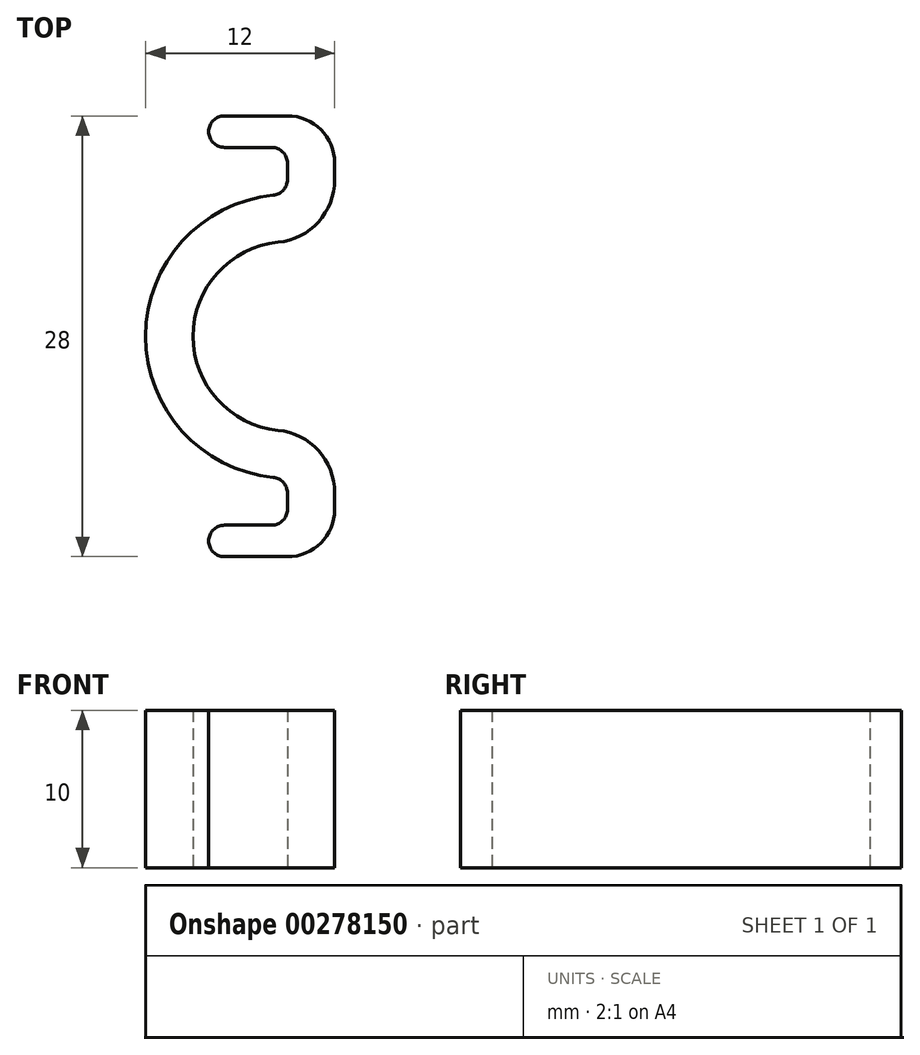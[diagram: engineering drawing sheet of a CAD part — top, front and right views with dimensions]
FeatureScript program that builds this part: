
annotation { "Feature Type Name" : "Feature", "Feature Type Description" : "" }
export const myFeature = defineFeature(function(context is Context, id is Id, definition is map)
    precondition{}
    {
        {
            var Q0;
            Q0=qCreatedBy(makeId("Top.planeOp"),FACE);
            var sketch = newSketch(context, id + "F0", { "sketchPlane" : qUnion([Q0])});
            skArc(sketch, "E0", {"start": v(0, 6) * mm, "mid": v(-6, 0) * mm, "end": v(0, -6) * mm});
            skArc(sketch, "E1.0", {"start": v(0, 9) * mm, "mid": v(-9, 0) * mm, "end": v(0, -9) * mm});
            skLineSegment(sketch, "E2", {"start": v(0, 9) * mm, "end": v(0, 6) * mm});
            skLineSegment(sketch, "E3", {"start": v(0, -6) * mm, "end": v(0, -9) * mm});
            skLineSegment(sketch, "E4.bottom", {"start": v(0, 6) * mm, "end": v(3, 6) * mm});
            skLineSegment(sketch, "E4.top", {"start": v(0, 14) * mm, "end": v(3, 14) * mm});
            skLineSegment(sketch, "E4.left", {"start": v(0, 6) * mm, "end": v(0, 14) * mm});
            skLineSegment(sketch, "E4.right", {"start": v(3, 6) * mm, "end": v(3, 14) * mm});
            skLineSegment(sketch, "E5.bottom", {"start": v(0, 14) * mm, "end": v(-5, 14) * mm});
            skLineSegment(sketch, "E5.top", {"start": v(0, 12) * mm, "end": v(-5, 12) * mm});
            skLineSegment(sketch, "E5.left", {"start": v(0, 14) * mm, "end": v(0, 12) * mm});
            skLineSegment(sketch, "E5.right", {"start": v(-5, 14) * mm, "end": v(-5, 12) * mm});
            skLineSegment(sketch, "E6.bottom", {"start": v(0, -6) * mm, "end": v(3, -6) * mm});
            skLineSegment(sketch, "E6.top", {"start": v(0, -14) * mm, "end": v(3, -14) * mm});
            skLineSegment(sketch, "E6.left", {"start": v(0, -6) * mm, "end": v(0, -14) * mm});
            skLineSegment(sketch, "E6.right", {"start": v(3, -6) * mm, "end": v(3, -14) * mm});
            skLineSegment(sketch, "E7.bottom", {"start": v(0, -14) * mm, "end": v(-5, -14) * mm});
            skLineSegment(sketch, "E7.top", {"start": v(0, -12) * mm, "end": v(-5, -12) * mm});
            skLineSegment(sketch, "E7.left", {"start": v(0, -14) * mm, "end": v(0, -12) * mm});
            skLineSegment(sketch, "E7.right", {"start": v(-5, -14) * mm, "end": v(-5, -12) * mm});
            skSolve(sketch);
        }
        {
            var Q0;
            {var subQ0=sQuery(id+"F0.wireOp",EDGE,"E0");Q0=makeQuery(id+"F0.imprint","IMPRINT",FACE,{"disambiguationData":[TD([[makeQuery(id+"F0.imprint","IMPRINT",EDGE,{"derivedFrom":subQ0}),-1.0]])]});}
            var Q1;
            {var subQ3=sQuery(id+"F0.wireOp",EDGE,"E4.bottom");Q1=makeQuery(id+"F0.imprint","IMPRINT",FACE,{"disambiguationData":[TD([[makeQuery(id+"F0.imprint","IMPRINT",EDGE,{"derivedFrom":subQ3}),1.0]])]});}
            var Q2;
            Q2=makeQuery(id+"F0.imprint","IMPRINT",FACE,{"disambiguationData":[TD([[makeQuery(id+"F0.imprint","IMPRINT",EDGE,{"derivedFrom":sQuery(id+"F0.wireOp",EDGE,"E5.bottom")}),1.0]])]});
            var Q3;
            {var subQ3=sQuery(id+"F0.wireOp",EDGE,"E6.bottom");Q3=makeQuery(id+"F0.imprint","IMPRINT",FACE,{"disambiguationData":[TD([[makeQuery(id+"F0.imprint","IMPRINT",EDGE,{"derivedFrom":subQ3}),-1.0]])]});}
            var Q4;
            Q4=makeQuery(id+"F0.imprint","IMPRINT",FACE,{"disambiguationData":[TD([[makeQuery(id+"F0.imprint","IMPRINT",EDGE,{"derivedFrom":sQuery(id+"F0.wireOp",EDGE,"E7.bottom")}),-1.0]])]});
            extrude(context, id + "F1", {"entities" : qUnion([Q0, Q1, Q2, Q3, Q4]), "depth" : 10 * mm});
        }
        {
            var Q0;
            Q0=makeQuery(id+"F1.opExtrude","SWEPT_EDGE",EDGE,{"disambiguationData":[OSD([sQuery(id+"F0.wireOp",EDGE,"E6.bottom"),sQuery(id+"F0.wireOp",EDGE,"E6.right")])]});
            var Q1;
            Q1=makeQuery(id+"F1.opExtrude","SWEPT_EDGE",EDGE,{"disambiguationData":[OSD([sQuery(id+"F0.wireOp",EDGE,"E4.bottom"),sQuery(id+"F0.wireOp",EDGE,"E4.right")])]});
            fillet(context, id + "F2", {"entities" : qUnion([Q0, Q1]), "radius" : 4 * mm, "tangentPropagation" : true, "allowEdgeOverflow" : false});
        }
        {
            var Q0;
            Q0=makeQuery(id+"F1.opExtrude","SWEPT_EDGE",EDGE,{"disambiguationData":[OSD([sQuery(id+"F0.wireOp",EDGE,"E6.top"),sQuery(id+"F0.wireOp",EDGE,"E6.right")])]});
            var Q1;
            Q1=makeQuery(id+"F1.opExtrude","SWEPT_EDGE",EDGE,{"disambiguationData":[OSD([sQuery(id+"F0.wireOp",EDGE,"E4.top"),sQuery(id+"F0.wireOp",EDGE,"E4.right")])]});
            fillet(context, id + "F3", {"entities" : qUnion([Q0, Q1]), "radius" : 3 * mm, "tangentPropagation" : true, "allowEdgeOverflow" : false});
        }
        {
            var Q0;
            Q0=makeQuery(id+"F1.opExtrude","SWEPT_EDGE",EDGE,{"disambiguationData":[OSD([sQuery(id+"F0.wireOp",EDGE,"E4.left"),sQuery(id+"F0.wireOp",EDGE,"E5.top"),sQuery(id+"F0.wireOp",EDGE,"E5.left")])]});
            var Q1;
            Q1=makeQuery(id+"F1.opExtrude","SWEPT_EDGE",EDGE,{"disambiguationData":[OSD([sQuery(id+"F0.wireOp",EDGE,"E6.left"),sQuery(id+"F0.wireOp",EDGE,"E7.top"),sQuery(id+"F0.wireOp",EDGE,"E7.left")])]});
            fillet(context, id + "F4", {"entities" : qUnion([Q0, Q1]), "radius" : 1 * mm, "tangentPropagation" : true, "allowEdgeOverflow" : false});
        }
        {
            var Q0;
            Q0=makeQuery(id+"F1.opExtrude","SWEPT_EDGE",EDGE,{"disambiguationData":[OSD([sQuery(id+"F0.wireOp",EDGE,"E1.0"),sQuery(id+"F0.wireOp",EDGE,"E4.left")])]});
            var Q1;
            Q1=makeQuery(id+"F1.opExtrude","SWEPT_EDGE",EDGE,{"disambiguationData":[OSD([sQuery(id+"F0.wireOp",EDGE,"E1.0"),sQuery(id+"F0.wireOp",EDGE,"E6.left")])]});
            fillet(context, id + "F5", {"entities" : qUnion([Q0, Q1]), "radius" : 1 * mm, "tangentPropagation" : true, "allowEdgeOverflow" : false});
        }
        {
            var Q0;
            Q0=makeQuery(id+"F1.opExtrude","SWEPT_EDGE",EDGE,{"disambiguationData":[OSD([sQuery(id+"F0.wireOp",EDGE,"E5.top"),sQuery(id+"F0.wireOp",EDGE,"E5.right")])]});
            var Q1;
            Q1=makeQuery(id+"F1.opExtrude","SWEPT_EDGE",EDGE,{"disambiguationData":[OSD([sQuery(id+"F0.wireOp",EDGE,"E5.bottom"),sQuery(id+"F0.wireOp",EDGE,"E5.right")])]});
            var Q2;
            Q2=makeQuery(id+"F1.opExtrude","SWEPT_EDGE",EDGE,{"disambiguationData":[OSD([sQuery(id+"F0.wireOp",EDGE,"E7.top"),sQuery(id+"F0.wireOp",EDGE,"E7.right")])]});
            var Q3;
            Q3=makeQuery(id+"F1.opExtrude","SWEPT_EDGE",EDGE,{"disambiguationData":[OSD([sQuery(id+"F0.wireOp",EDGE,"E7.bottom"),sQuery(id+"F0.wireOp",EDGE,"E7.right")])]});
            fillet(context, id + "F6", {"entities" : qUnion([Q0, Q1, Q2, Q3]), "radius" : 1 * mm, "tangentPropagation" : true, "allowEdgeOverflow" : false});
        }
    });
